# Revit family: B 3003 BOW
name_source: partatom
category: Lighting Fixtures
revit_build: Autodesk Revit 2017 (Build: 20160225_1515(x64)
units: mm (PartAtom-declared; Revit-internal decimal feet)

## family parameters
Always vertical = Yes
Cut with Voids When Loaded = No
Light Source = Yes
OmniClass Number = 23.80.70.00
OmniClass Title = Lighting
Part Type = Normal
Room Calculation Point = No
Round Connector Dimension = Use Diameter
Shared = No
Work Plane-Based = No

## types (2) — shared parameters
Apparent Load = 135 VA
Color Filter = 16777215
Dimming Lamp Color Temperature Shift = <None>
Emit Shape Visible in Rendering = Yes
Emit from Circle Diameter = 370 mm  [stored 1.21391 ft]
Light Source Symbol Size = 610 mm
Manufacturer = ARLIGHT
Type Image = B 3003 BOW.JPG
Wattage Comments = 3x46W

## per-type parameters (varying)
| type | Type Comments |
| BBOW.3003.138.30 | 3X46W 3000K |
| BBOW.3003.138.40 | 3X46W 4000K |

note: [stored X ft] marks values corroborated as IEEE doubles in the binary element streams (Revit-internal decimal feet)

## geometry (parser evidence)
native form markers: Sweep x5
no freeform markers — native parametric forms only
